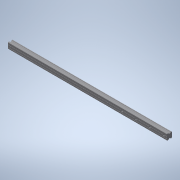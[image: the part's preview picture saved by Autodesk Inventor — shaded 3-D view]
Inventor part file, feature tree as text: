
AUTODESK INVENTOR PART (.ipt)
format: ipt  version: 2022 (Build 260153000, 153)  size: 163,328 bytes
history: native  units: mm (DEFAULTED — no unit token found)
features: other x21, sketch x2, extrude x1, hole x1, pattern_linear x1
ambient origin geometry x8: Origin, YZ Plane, XZ Plane, XY Plane, X Axis, Y Axis, Z Axis, Center Point
bodies: Solid1 (feature_tree)
feature tree (26):
  extrude  "Extrusion1"  Depth=10.0mm TaperAngle=0.0deg
  hole  "Hole1"  [1 undecoded]
  pattern_linear  "Rectangular Pattern1"  [2 undecoded]
  other  "4dummy_XY"
  other  "4dummy_YZ"
  other  "4dummy_ZX"
  other  "4dummy_X"
  other  "4dummy_Y"
  other  "4dummy_Z"
  other  "4dummy_Center"
  other  "4slide_XY"
  other  "4slide_YZ"
  other  "4slide_ZX"
  other  "4slide_X"
  other  "4slide_Y"
  other  "4slide_Z"
  other  "4slide_Center"
  other  "4track_XY"
  other  "4track_YZ"
  other  "4track_ZX"
  other  "4track_X"
  other  "4track_Y"
  other  "4track_Z"
  other  "4track_Center"
  sketch  "Sketch_18"  dims[d2=9.0mm d3=6.0mm d4=14.0mm d5=12.0mm d6=90.0deg d7=29.0mm d8=0.0mm d9=40.0mm d11=80.0mm d12=10.0mm d14=0.0mm d15=0.0mm]
  sketch  "Sketch2"  dims[d0=914.4mm d1=0.0mm]
note: 3 required parameter values undecoded (feature->parameter linkage not recoverable at this tier; creation-order binding heuristic only, values carry confidence <= 0.55)
